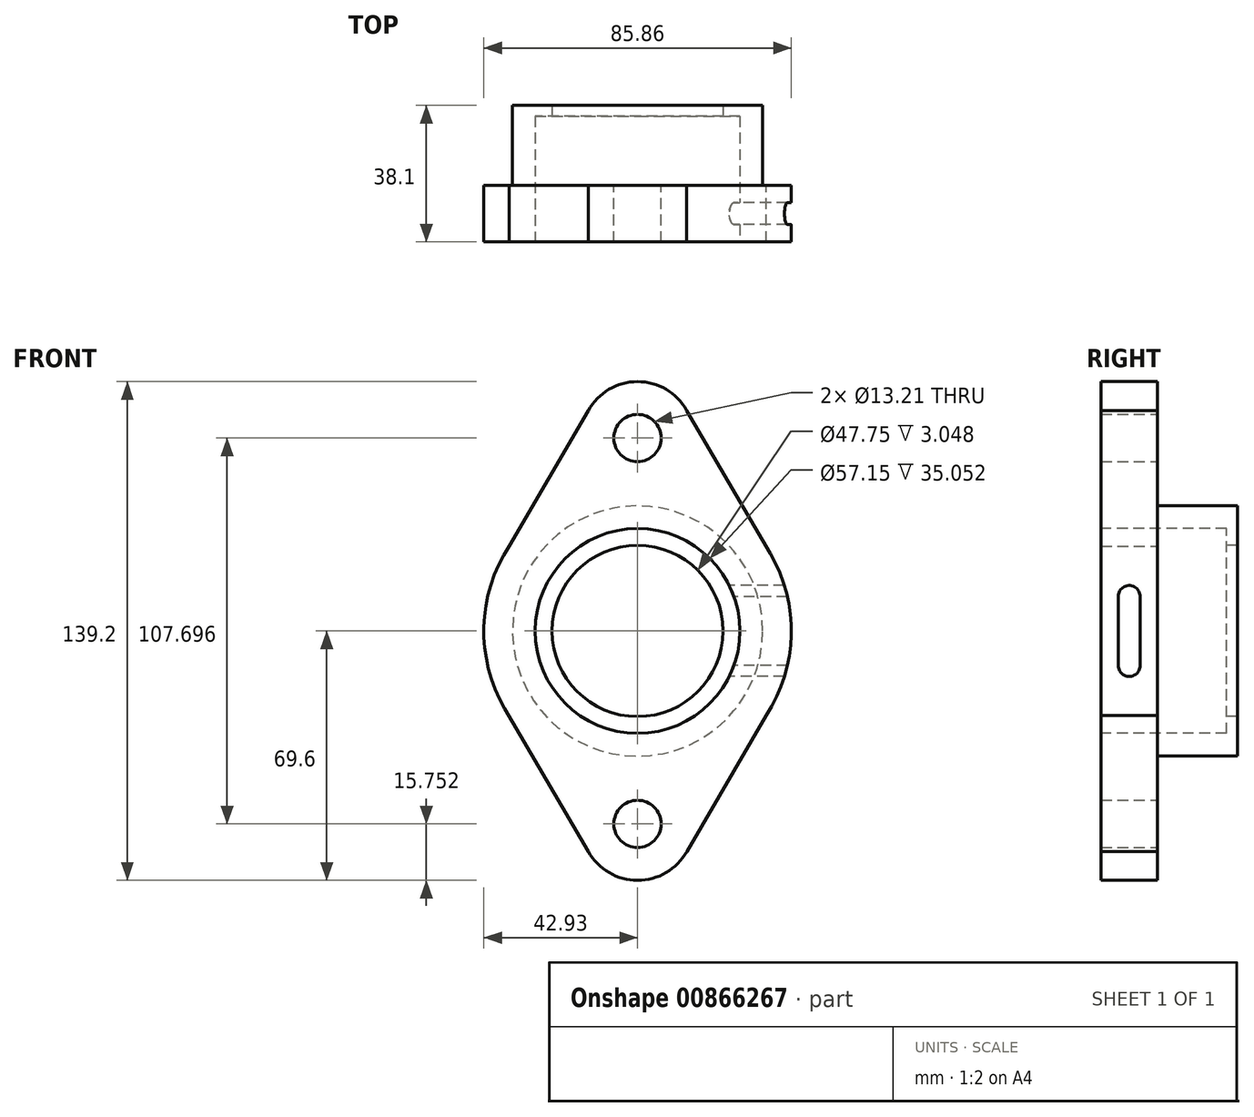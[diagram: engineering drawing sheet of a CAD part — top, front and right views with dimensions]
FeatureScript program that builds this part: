
annotation { "Feature Type Name" : "Feature", "Feature Type Description" : "" }
export const myFeature = defineFeature(function(context is Context, id is Id, definition is map)
    precondition{}
    {
        {
            var Q0;
            Q0=qCreatedBy(makeId("Front.planeOp"),FACE);
            var sketch = newSketch(context, id + "F0", { "sketchPlane" : qUnion([Q0])});
            skCircle(sketch, "E0", {"center": v(0, 0) * mm, "radius": 42.93 * mm});
            skLineSegment(sketch, "E1", {"start": v(0, 0) * mm, "end": v(0, 53.85) * mm});
            skLineSegment(sketch, "E2", {"start": v(0, 0) * mm, "end": v(0, -53.85) * mm});
            skCircle(sketch, "E3", {"center": v(0, 53.85) * mm, "radius": 15.75 * mm});
            skCircle(sketch, "E4", {"center": v(0, -53.85) * mm, "radius": 15.75 * mm});
            skCircle(sketch, "E5", {"center": v(0, -53.85) * mm, "radius": 6.6 * mm});
            skCircle(sketch, "E6", {"center": v(0, 53.85) * mm, "radius": 6.6 * mm});
            skLineSegment(sketch, "E7", {"start": v(-13.45, 62.03) * mm, "end": v(-38.27, 19.44) * mm});
            skLineSegment(sketch, "E8", {"start": v(13.45, 62.03) * mm, "end": v(38.36, 19.44) * mm});
            skLineSegment(sketch, "E9", {"start": v(-13.45, -62.03) * mm, "end": v(-38.27, -19.59) * mm});
            skLineSegment(sketch, "E10", {"start": v(13.45, -62.03) * mm, "end": v(38.2, -19.59) * mm});
            skSolve(sketch);
        }
        {
            var Q0;
            Q0=qSketchRegion(id+"F0",true);
            var Q1;
            {var subQ0=sQuery(id+"F0.wireOp",EDGE,"E1");var subQ1=sQuery(id+"F0.wireOp",EDGE,"E0");var subQ2=makeQuery(id+"F0.imprint","INTERSECT",VERTEX,{"derivedFrom":[subQ1,subQ0]});Q1=makeQuery(id+"F0.imprint","IMPRINT",FACE,{"disambiguationData":[TD([[makeQuery(id+"F0.imprint","IMPRINT",EDGE,{"disambiguationData":[TD([[subQ2,-1.0]])],"derivedFrom":subQ1}),1.0]])]});}
            var Q2;
            {var subQ0=sQuery(id+"F0.wireOp",EDGE,"E1");var subQ1=sQuery(id+"F0.wireOp",EDGE,"E0");var subQ2=makeQuery(id+"F0.imprint","INTERSECT",VERTEX,{"derivedFrom":[subQ1,subQ0]});Q2=makeQuery(id+"F0.imprint","IMPRINT",FACE,{"disambiguationData":[TD([[makeQuery(id+"F0.imprint","IMPRINT",EDGE,{"disambiguationData":[TD([[subQ2,1.0]])],"derivedFrom":subQ1}),1.0]])]});}
            var Q3;
            {var subQ0=sQuery(id+"F0.wireOp",EDGE,"E2");var subQ1=sQuery(id+"F0.wireOp",EDGE,"E0");var subQ2=makeQuery(id+"F0.imprint","INTERSECT",VERTEX,{"derivedFrom":[subQ1,subQ0]});Q3=makeQuery(id+"F0.imprint","IMPRINT",FACE,{"disambiguationData":[TD([[makeQuery(id+"F0.imprint","IMPRINT",EDGE,{"disambiguationData":[TD([[subQ2,1.0]])],"derivedFrom":subQ1}),1.0]])]});}
            var Q4;
            {var subQ0=sQuery(id+"F0.wireOp",EDGE,"E2");var subQ1=sQuery(id+"F0.wireOp",EDGE,"E0");var subQ2=makeQuery(id+"F0.imprint","INTERSECT",VERTEX,{"derivedFrom":[subQ1,subQ0]});Q4=makeQuery(id+"F0.imprint","IMPRINT",FACE,{"disambiguationData":[TD([[makeQuery(id+"F0.imprint","IMPRINT",EDGE,{"disambiguationData":[TD([[subQ2,-1.0]])],"derivedFrom":subQ1}),1.0]])]});}
            extrude(context, id + "F1", {"entities" : qUnion([Q0, Q1, Q2, Q3, Q4]), "depth" : 15.75 * mm, "offsetDistance" : 25.4 * mm});
        }
        {
            var Q0;
            Q0=makeQuery(id+"F1.opExtrude","CAP_FACE",FACE,{"disambiguationData":[OSD([sQuery(id+"F0.wireOp",EDGE,"E0"),sQuery(id+"F0.wireOp",EDGE,"E3"),sQuery(id+"F0.wireOp",EDGE,"E4"),sQuery(id+"F0.wireOp",EDGE,"E5"),sQuery(id+"F0.wireOp",EDGE,"E6"),sQuery(id+"F0.wireOp",EDGE,"E7"),sQuery(id+"F0.wireOp",EDGE,"E8"),sQuery(id+"F0.wireOp",EDGE,"E9"),sQuery(id+"F0.wireOp",EDGE,"E10")])],"isStart":false});
            var sketch = newSketch(context, id + "F2", { "sketchPlane" : qUnion([Q0])});
            skCircle(sketch, "E11", {"center": v(0, 0) * mm, "radius": 34.93 * mm});
            skSolve(sketch);
        }
        {
            var Q0;
            Q0=makeQuery(id+"F2.imprint","IMPRINT",FACE,{"disambiguationData":[TD([[makeQuery(id+"F2.imprint","IMPRINT",EDGE,{"derivedFrom":sQuery(id+"F2.wireOp",EDGE,"E11")}),1.0]])]});
            extrude(context, id + "F3", {"entities" : qUnion([Q0]), "operationType" : NewBodyOperationType.ADD, "oppositeDirection" : true, "depth" : 38.1 * mm, "offsetDistance" : 25.4 * mm});
        }
        {
            var Q0;
            Q0=makeQuery(id+"F1.opExtrude","CAP_FACE",FACE,{"disambiguationData":[OSD([sQuery(id+"F0.wireOp",EDGE,"E0"),sQuery(id+"F0.wireOp",EDGE,"E3"),sQuery(id+"F0.wireOp",EDGE,"E4"),sQuery(id+"F0.wireOp",EDGE,"E5"),sQuery(id+"F0.wireOp",EDGE,"E6"),sQuery(id+"F0.wireOp",EDGE,"E7"),sQuery(id+"F0.wireOp",EDGE,"E8"),sQuery(id+"F0.wireOp",EDGE,"E9"),sQuery(id+"F0.wireOp",EDGE,"E10")])],"isStart":false});
            var sketch = newSketch(context, id + "F4", { "sketchPlane" : qUnion([Q0])});
            skCircle(sketch, "E12", {"center": v(0, 0) * mm, "radius": 23.88 * mm});
            skSolve(sketch);
        }
        {
            var Q0;
            Q0=makeQuery(id+"F4.imprint","IMPRINT",FACE,{"disambiguationData":[TD([[makeQuery(id+"F4.imprint","IMPRINT",EDGE,{"derivedFrom":sQuery(id+"F4.wireOp",EDGE,"E12")}),1.0]])]});
            extrude(context, id + "F5", {"entities" : qUnion([Q0]), "operationType" : NewBodyOperationType.ADD, "oppositeDirection" : true, "depth" : 38.1 * mm, "offsetDistance" : 25.4 * mm});
        }
        {
            var Q0;
            Q0=makeQuery(id+"F1.opExtrude","CAP_FACE",FACE,{"disambiguationData":[OSD([sQuery(id+"F0.wireOp",EDGE,"E0"),sQuery(id+"F0.wireOp",EDGE,"E3"),sQuery(id+"F0.wireOp",EDGE,"E4"),sQuery(id+"F0.wireOp",EDGE,"E5"),sQuery(id+"F0.wireOp",EDGE,"E6"),sQuery(id+"F0.wireOp",EDGE,"E7"),sQuery(id+"F0.wireOp",EDGE,"E8"),sQuery(id+"F0.wireOp",EDGE,"E9"),sQuery(id+"F0.wireOp",EDGE,"E10")])],"isStart":false});
            var sketch = newSketch(context, id + "F6", { "sketchPlane" : qUnion([Q0])});
            skCircle(sketch, "E13", {"center": v(0, 0) * mm, "radius": 23.88 * mm});
            skSolve(sketch);
        }
        {
            var Q0;
            Q0=makeQuery(id+"F6.imprint","IMPRINT",FACE,{"disambiguationData":[TD([[makeQuery(id+"F6.imprint","IMPRINT",EDGE,{"derivedFrom":sQuery(id+"F6.wireOp",EDGE,"E13")}),1.0]])]});
            extrude(context, id + "F7", {"entities" : qUnion([Q0]), "operationType" : NewBodyOperationType.REMOVE, "oppositeDirection" : true, "depth" : 38.1 * mm, "offsetDistance" : 25.4 * mm});
        }
        {
            var Q0;
            Q0=qCreatedBy(makeId("Right.planeOp"),FACE);
            var sketch = newSketch(context, id + "F8", { "sketchPlane" : qUnion([Q0])});
            skLineSegment(sketch, "E14", {"start": v(-7.87, 0) * mm, "end": v(-7.87, -9.65) * mm});
            skLineSegment(sketch, "E15", {"start": v(-7.87, 0) * mm, "end": v(-7.87, 9.65) * mm});
            skCircle(sketch, "E16", {"center": v(-7.87, -9.65) * mm, "radius": 3.05 * mm});
            skCircle(sketch, "E17", {"center": v(-7.87, 9.65) * mm, "radius": 3.05 * mm});
            skLineSegment(sketch, "E18", {"start": v(-10.92, -9.76) * mm, "end": v(-10.92, 9.65) * mm});
            skLineSegment(sketch, "E19", {"start": v(-4.83, -9.76) * mm, "end": v(-4.83, 9.54) * mm});
            skSolve(sketch);
        }
        {
            var Q0;
            Q0=qSketchRegion(id+"F8",true);
            extrude(context, id + "F9", {"entities" : qUnion([Q0]), "operationType" : NewBodyOperationType.REMOVE, "depth" : 50.8 * mm, "offsetDistance" : 25.4 * mm});
        }
        {
            var Q0;
            Q0=makeQuery(id+"F1.opExtrude","CAP_FACE",FACE,{"disambiguationData":[OSD([sQuery(id+"F0.wireOp",EDGE,"E0"),sQuery(id+"F0.wireOp",EDGE,"E3"),sQuery(id+"F0.wireOp",EDGE,"E4"),sQuery(id+"F0.wireOp",EDGE,"E5"),sQuery(id+"F0.wireOp",EDGE,"E6"),sQuery(id+"F0.wireOp",EDGE,"E7"),sQuery(id+"F0.wireOp",EDGE,"E8"),sQuery(id+"F0.wireOp",EDGE,"E9"),sQuery(id+"F0.wireOp",EDGE,"E10")])],"isStart":false});
            var sketch = newSketch(context, id + "F10", { "sketchPlane" : qUnion([Q0])});
            skCircle(sketch, "E20", {"center": v(0, 0) * mm, "radius": 28.58 * mm});
            skCircle(sketch, "E21", {"center": v(0, 0) * mm, "radius": 34.93 * mm});
            skSolve(sketch);
        }
        {
            var Q0;
            Q0=makeQuery(id+"F10.imprint","IMPRINT",FACE,{"disambiguationData":[TD([[makeQuery(id+"F10.imprint","IMPRINT",EDGE,{"derivedFrom":sQuery(id+"F10.wireOp",EDGE,"E20")}),1.0]])]});
            extrude(context, id + "F11", {"entities" : qUnion([Q0]), "operationType" : NewBodyOperationType.REMOVE, "oppositeDirection" : true, "depth" : 35.05 * mm, "offsetDistance" : 25.4 * mm});
        }
    });
